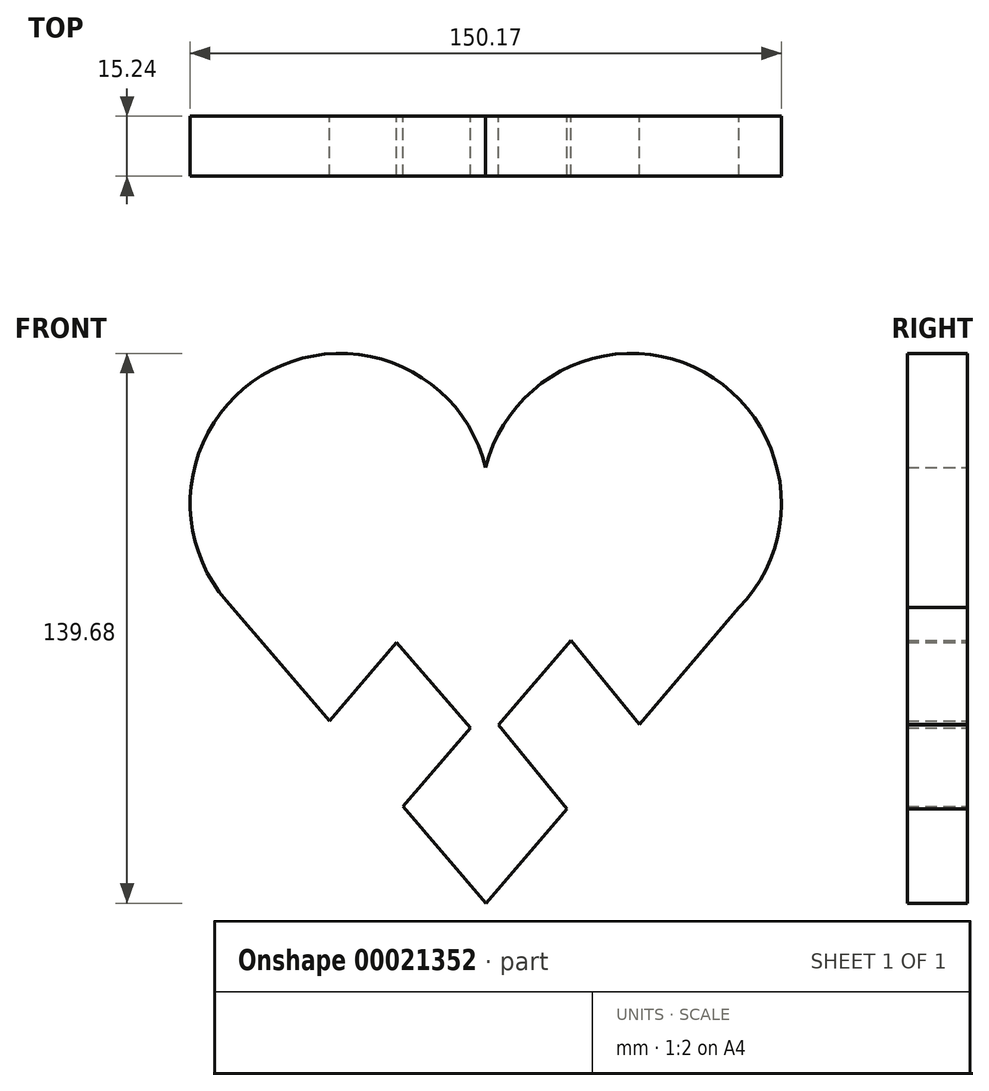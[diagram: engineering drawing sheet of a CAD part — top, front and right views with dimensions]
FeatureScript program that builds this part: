
annotation { "Feature Type Name" : "Feature", "Feature Type Description" : "" }
export const myFeature = defineFeature(function(context is Context, id is Id, definition is map)
    precondition{}
    {
        {
            var Q0;
            Q0=qCreatedBy(makeId("Front.planeOp"),FACE);
            var sketch = newSketch(context, id + "F0", { "sketchPlane" : qUnion([Q0])});
            skArc(sketch, "E0", {"start": v(-0.07, 41.72) * mm, "mid": v(-54.52, 66.43) * mm, "end": v(-65.95, 7.73) * mm});
            skArc(sketch, "E1", {"start": v(64.31, 6.09) * mm, "mid": v(55.37, 65.9) * mm, "end": v(-0.07, 41.72) * mm});
            skLineSegment(sketch, "E2", {"start": v(65.81, 7.73) * mm, "end": v(65.81, 7.73) * mm});
            skLineSegment(sketch, "E3", {"start": v(-65.95, 7.73) * mm, "end": v(-39.81, -22.68) * mm});
            skLineSegment(sketch, "E4", {"start": v(0, -69) * mm, "end": v(20.54, -45.05) * mm});
            skLineSegment(sketch, "E5", {"start": v(-21.08, -44.48) * mm, "end": v(-3.97, -24.53) * mm, "construction": true});
            skLineSegment(sketch, "E6", {"start": v(3.14, -23.74) * mm, "end": v(20.54, -45.05) * mm, "construction": true});
            skLineSegment(sketch, "E7", {"start": v(-3.97, -24.53) * mm, "end": v(-22.7, -2.73) * mm, "construction": true});
            skLineSegment(sketch, "E8", {"start": v(3.14, -23.74) * mm, "end": v(21.53, -2.3) * mm, "construction": true});
            skLineSegment(sketch, "E9", {"start": v(-22.7, -2.73) * mm, "end": v(-39.81, -22.68) * mm});
            skLineSegment(sketch, "E10", {"start": v(-22.7, -2.73) * mm, "end": v(-3.97, -24.53) * mm});
            skLineSegment(sketch, "E11", {"start": v(-3.97, -24.53) * mm, "end": v(-21.08, -44.48) * mm});
            skLineSegment(sketch, "E12", {"start": v(3.14, -23.74) * mm, "end": v(21.53, -2.3) * mm});
            skLineSegment(sketch, "E13", {"start": v(3.14, -23.74) * mm, "end": v(20.54, -45.05) * mm});
            skLineSegment(sketch, "E14", {"start": v(21.53, -2.3) * mm, "end": v(38.94, -23.6) * mm});
            skPoint(sketch, "E15.start.orphan", {"position": v(-87.73, 7.73) * mm});
            skPoint(sketch, "E16.orphan", {"position": v(84.67, 7.73) * mm});
            skPoint(sketch, "E17.end.orphan", {"position": v(0, 7.73) * mm});
            skPoint(sketch, "E18.orphan", {"position": v(0, -19.9) * mm});
            skLineSegment(sketch, "E19.trimOffspring", {"start": v(-21.08, -44.48) * mm, "end": v(0, -69) * mm});
            skLineSegment(sketch, "E20", {"start": v(38.94, -23.6) * mm, "end": v(67.34, 9.63) * mm});
            skSolve(sketch);
        }
        {
            var Q0;
            Q0 = qSketchRegion(id + "F0", true);
            extrude(context, id + "F1", {"entities" : qUnion([Q0]), "depth" : 15.24 * mm});
        }
    });
